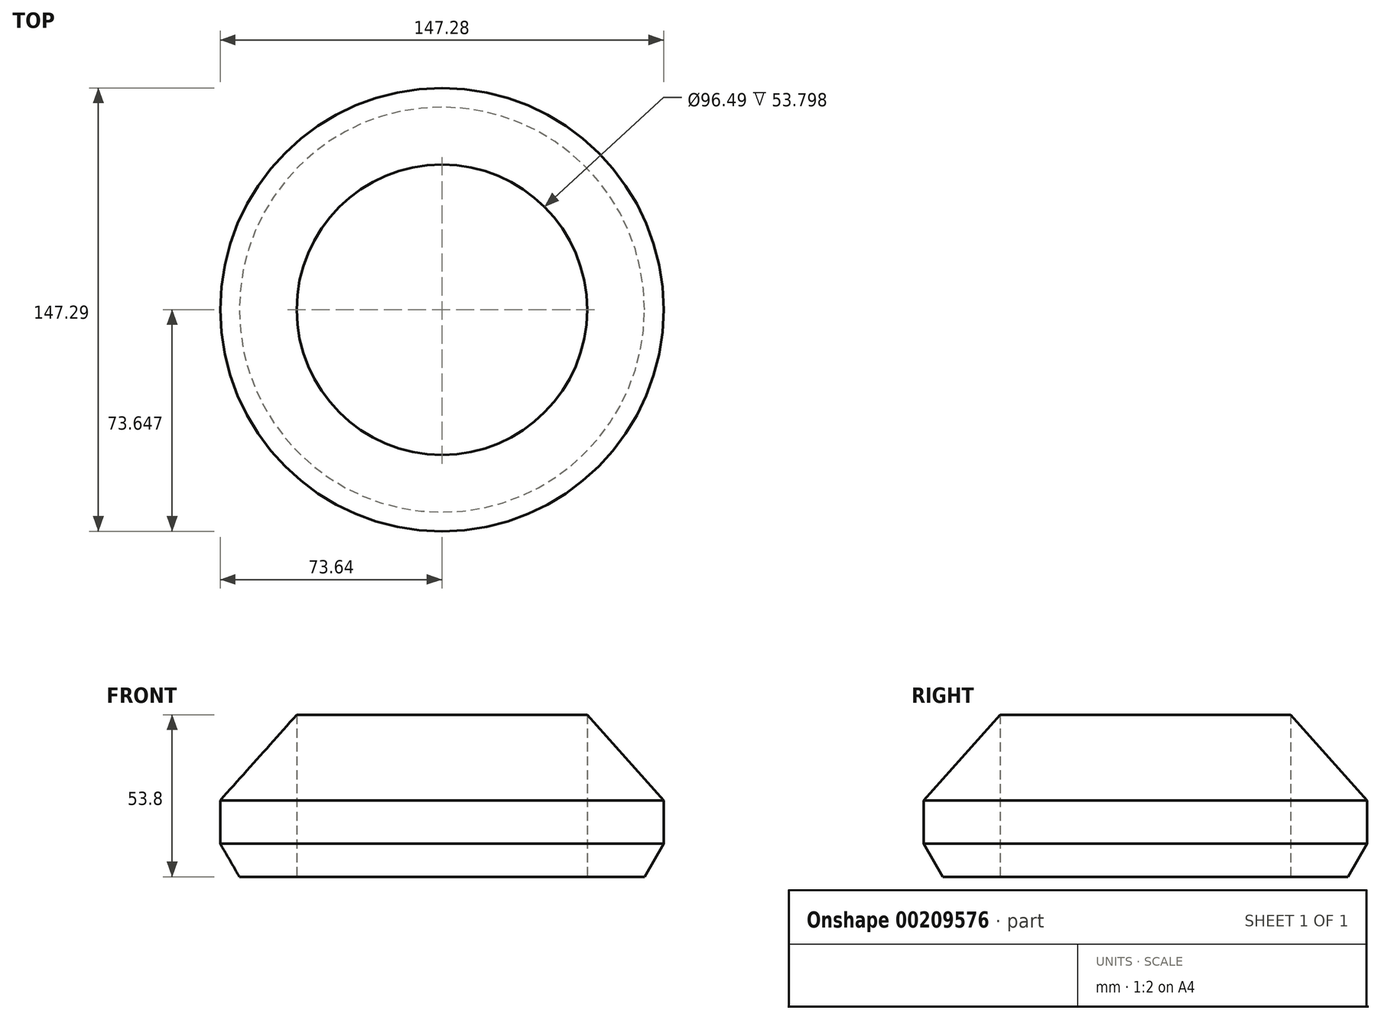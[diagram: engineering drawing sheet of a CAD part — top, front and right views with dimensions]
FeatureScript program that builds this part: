
annotation { "Feature Type Name" : "Feature", "Feature Type Description" : "" }
export const myFeature = defineFeature(function(context is Context, id is Id, definition is map)
    precondition{}
    {
        {
            var Q0;
            Q0=qCreatedBy(makeId("Right.planeOp"),FACE);
            var sketch = newSketch(context, id + "F0", { "sketchPlane" : qUnion([Q0])});
            skLineSegment(sketch, "E0.bottom", {"start": v(0, 0) * mm, "end": v(25.4, 0) * mm});
            skLineSegment(sketch, "E0.top", {"start": v(0, 25.4) * mm, "end": v(25.4, 25.4) * mm});
            skLineSegment(sketch, "E0.left", {"start": v(0, 0) * mm, "end": v(0, 25.4) * mm});
            skLineSegment(sketch, "E0.right", {"start": v(25.4, 0) * mm, "end": v(25.4, 25.4) * mm});
            skLineSegment(sketch, "E1", {"start": v(0, 25.4) * mm, "end": v(0, 53.8) * mm});
            skLineSegment(sketch, "E2", {"start": v(0, 53.8) * mm, "end": v(25.4, 25.4) * mm});
            skLineSegment(sketch, "E3", {"start": v(0, 0) * mm, "end": v(0, 87.2) * mm, "construction": true});
            skLineSegment(sketch, "E4", {"start": v(-48.24, 0) * mm, "end": v(-48.24, 87.5) * mm, "construction": true});
            skSolve(sketch);
        }
        {
            var Q0;
            Q0 = qSketchRegion(id + "F0", true);
            var Q1;
            Q1=sQuery(id+"F0.wireOp",EDGE,"E4");
            revolve(context, id + "F1", {"entities" : qUnion([Q0]), "axis" : qUnion([Q1]), "revolveType" : RevolveType.FULL});
        }
        {
            var Q0;
            Q0=makeQuery(id+"F1.opRevolve","SWEPT_EDGE",EDGE,{"disambiguationData":[OSD([sQuery(id+"F0.wireOp",EDGE,"E0.bottom"),sQuery(id+"F0.wireOp",EDGE,"E0.right")])]});
            chamfer(context, id + "F2", {"entities" : qUnion([Q0]), "chamferType" : ChamferType.OFFSET_ANGLE, "width" : 6.35 * mm, "oppositeDirection" : false, "angle" : 60 * degree, "tangentPropagation" : true});
        }
    });
